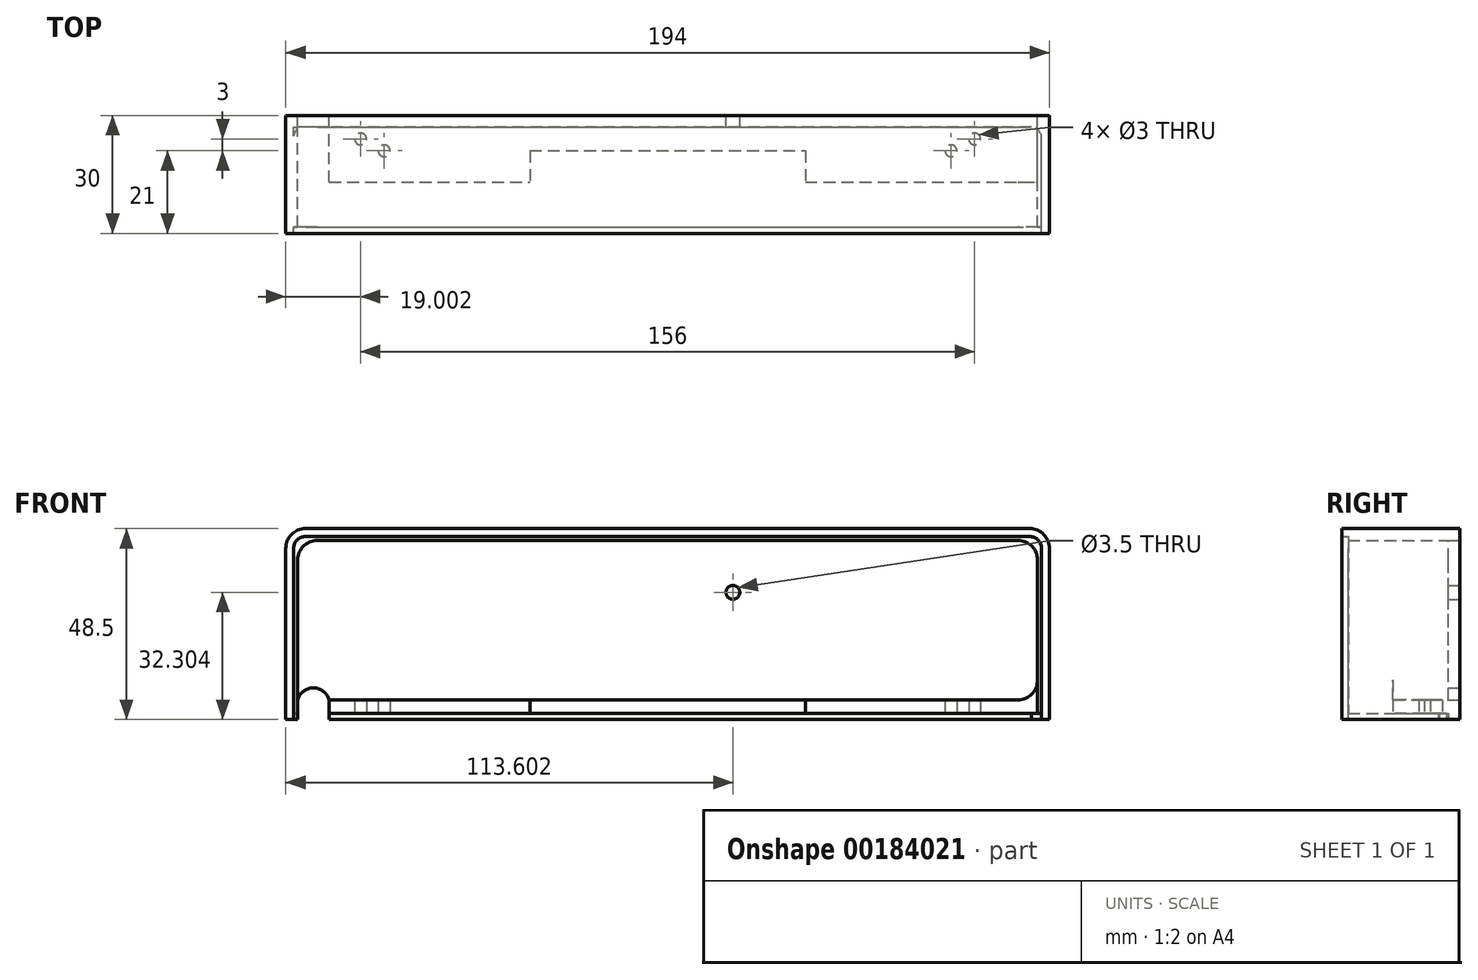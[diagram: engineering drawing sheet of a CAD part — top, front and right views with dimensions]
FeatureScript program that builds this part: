
annotation { "Feature Type Name" : "Feature", "Feature Type Description" : "" }
export const myFeature = defineFeature(function(context is Context, id is Id, definition is map)
    precondition{}
    {
        {
            var Q0;
            Q0=qCreatedBy(makeId("Front.planeOp"),FACE);
            var sketch = newSketch(context, id + "F0", { "sketchPlane" : qUnion([Q0])});
            skLineSegment(sketch, "E0", {"start": v(-180.48, -72.77) * mm, "end": v(-180.48, -29.27) * mm});
            skLineSegment(sketch, "E1", {"start": v(-175.48, -24.27) * mm, "end": v(8.52, -24.27) * mm});
            skLineSegment(sketch, "E2", {"start": v(13.52, -29.27) * mm, "end": v(13.52, -72.77) * mm});
            skLineSegment(sketch, "E3", {"start": v(13.52, -72.77) * mm, "end": v(11.52, -72.77) * mm});
            skLineSegment(sketch, "E4", {"start": v(11.52, -72.77) * mm, "end": v(11.52, -29.27) * mm});
            skLineSegment(sketch, "E5", {"start": v(-180.48, -72.77) * mm, "end": v(-177.48, -72.77) * mm});
            skLineSegment(sketch, "E6", {"start": v(-178.48, -72.77) * mm, "end": v(-178.48, -29.27) * mm});
            skLineSegment(sketch, "E7", {"start": v(-175.48, -26.27) * mm, "end": v(8.52, -26.27) * mm});
            skLineSegment(sketch, "E8", {"start": v(-169.48, -71.17) * mm, "end": v(11.52, -71.17) * mm});
            skLineSegment(sketch, "E9", {"start": v(-177.48, -72.77) * mm, "end": v(-177.48, -32.27) * mm});
            skLineSegment(sketch, "E10", {"start": v(-172.48, -27.27) * mm, "end": v(5.52, -27.27) * mm});
            skLineSegment(sketch, "E11", {"start": v(10.52, -62.77) * mm, "end": v(10.52, -32.27) * mm});
            skLineSegment(sketch, "E12", {"start": v(-169.48, -67.77) * mm, "end": v(5.52, -67.77) * mm});
            skLineSegment(sketch, "E13", {"start": v(-118.48, -71.17) * mm, "end": v(-118.48, -67.77) * mm});
            skLineSegment(sketch, "E14", {"start": v(-48.48, -71.17) * mm, "end": v(-48.48, -67.77) * mm});
            skLineSegment(sketch, "E15", {"start": v(-163.98, -67.77) * mm, "end": v(-163.98, -71.17) * mm});
            skLineSegment(sketch, "E16", {"start": v(-166.98, -67.77) * mm, "end": v(-166.98, -71.17) * mm});
            skLineSegment(sketch, "E17", {"start": v(-2.98, -67.77) * mm, "end": v(-2.98, -71.17) * mm});
            skLineSegment(sketch, "E18", {"start": v(0.02, -67.77) * mm, "end": v(0.02, -71.17) * mm});
            skArc(sketch, "E19", {"start": v(-175.48, -26.27) * mm, "mid": v(-177.6, -27.14) * mm, "end": v(-178.48, -29.27) * mm});
            skArc(sketch, "E20", {"start": v(11.52, -29.27) * mm, "mid": v(10.64, -27.14) * mm, "end": v(8.52, -26.27) * mm});
            skArc(sketch, "E21", {"start": v(-175.48, -24.27) * mm, "mid": v(-179.01, -25.73) * mm, "end": v(-180.48, -29.27) * mm});
            skArc(sketch, "E22", {"start": v(13.52, -29.27) * mm, "mid": v(12.06, -25.73) * mm, "end": v(8.52, -24.27) * mm});
            skLineSegment(sketch, "E23", {"start": v(-156.98, -71.17) * mm, "end": v(-156.98, -67.77) * mm});
            skLineSegment(sketch, "E24", {"start": v(-153.98, -71.17) * mm, "end": v(-153.98, -67.77) * mm});
            skLineSegment(sketch, "E25", {"start": v(-12.98, -67.77) * mm, "end": v(-12.98, -71.17) * mm});
            skLineSegment(sketch, "E26", {"start": v(-9.98, -67.77) * mm, "end": v(-9.98, -71.17) * mm});
            skLineSegment(sketch, "E27", {"start": v(11.52, -72.77) * mm, "end": v(-169.48, -72.77) * mm});
            skCircle(sketch, "E28", {"center": v(-66.88, -40.47) * mm, "radius": 1.75 * mm});
            skLineSegment(sketch, "E29", {"start": v(-169.48, -71.17) * mm, "end": v(-169.48, -67.77) * mm});
            skLineSegment(sketch, "E30", {"start": v(-169.48, -72.77) * mm, "end": v(-169.48, -67.77) * mm});
            skArc(sketch, "E31", {"start": v(-172.48, -27.27) * mm, "mid": v(-176.01, -28.73) * mm, "end": v(-177.48, -32.27) * mm});
            skArc(sketch, "E32", {"start": v(10.52, -32.27) * mm, "mid": v(9.06, -28.73) * mm, "end": v(5.52, -27.27) * mm});
            skArc(sketch, "E33", {"start": v(5.52, -67.77) * mm, "mid": v(9.06, -66.3) * mm, "end": v(10.52, -62.77) * mm});
            skArc(sketch, "E34", {"start": v(-169.48, -67.77) * mm, "mid": v(-173.48, -64.73) * mm, "end": v(-177.48, -67.77) * mm});
            skLineSegment(sketch, "E35", {"start": v(10.52, -62.77) * mm, "end": v(10.52, -71.17) * mm});
            skSolve(sketch);
        }
        {
            var Q0;
            {var subQ1=sQuery(id+"F0.wireOp",EDGE,"E0");Q0=makeQuery(id+"F0.imprint","IMPRINT",FACE,{"disambiguationData":[TD([[makeQuery(id+"F0.imprint","IMPRINT",EDGE,{"derivedFrom":subQ1}),-1.0]])]});}
            extrude(context, id + "F1", {"entities" : qUnion([Q0]), "depth" : 30 * mm});
        }
        {
            var Q0;
            {var subQ9=sQuery(id+"F0.wireOp",EDGE,"E6");Q0=makeQuery(id+"F0.imprint","IMPRINT",FACE,{"disambiguationData":[TD([[makeQuery(id+"F0.imprint","IMPRINT",EDGE,{"derivedFrom":subQ9}),-1.0]])]});}
            extrude(context, id + "F2", {"entities" : qUnion([Q0]), "operationType" : NewBodyOperationType.ADD, "depth" : 28.4 * mm});
        }
        {
            var Q0;
            {var subQ3=sQuery(id+"F0.wireOp",EDGE,"E16");Q0=makeQuery(id+"F0.imprint","IMPRINT",FACE,{"disambiguationData":[TD([[makeQuery(id+"F0.imprint","IMPRINT",EDGE,{"derivedFrom":subQ3}),-1.0]])]});}
            var Q1;
            {var subQ0=sQuery(id+"F0.wireOp",EDGE,"E15");Q1=makeQuery(id+"F0.imprint","IMPRINT",FACE,{"disambiguationData":[TD([[makeQuery(id+"F0.imprint","IMPRINT",EDGE,{"derivedFrom":subQ0}),-1.0]])]});}
            var Q2;
            {var subQ0=sQuery(id+"F0.wireOp",EDGE,"E15");Q2=makeQuery(id+"F0.imprint","IMPRINT",FACE,{"disambiguationData":[TD([[makeQuery(id+"F0.imprint","IMPRINT",EDGE,{"derivedFrom":subQ0}),1.0]])]});}
            var Q3;
            {var subQ0=sQuery(id+"F0.wireOp",EDGE,"E23");Q3=makeQuery(id+"F0.imprint","IMPRINT",FACE,{"disambiguationData":[TD([[makeQuery(id+"F0.imprint","IMPRINT",EDGE,{"derivedFrom":subQ0}),-1.0]])]});}
            var Q4;
            {var subQ0=sQuery(id+"F0.wireOp",EDGE,"E13");Q4=makeQuery(id+"F0.imprint","IMPRINT",FACE,{"disambiguationData":[TD([[makeQuery(id+"F0.imprint","IMPRINT",EDGE,{"derivedFrom":subQ0}),1.0]])]});}
            var Q5;
            {var subQ0=sQuery(id+"F0.wireOp",EDGE,"E13");Q5=makeQuery(id+"F0.imprint","IMPRINT",FACE,{"disambiguationData":[TD([[makeQuery(id+"F0.imprint","IMPRINT",EDGE,{"derivedFrom":subQ0}),-1.0]])]});}
            var Q6;
            {var subQ0=sQuery(id+"F0.wireOp",EDGE,"E14");Q6=makeQuery(id+"F0.imprint","IMPRINT",FACE,{"disambiguationData":[TD([[makeQuery(id+"F0.imprint","IMPRINT",EDGE,{"derivedFrom":subQ0}),-1.0]])]});}
            var Q7;
            {var subQ0=sQuery(id+"F0.wireOp",EDGE,"E25");Q7=makeQuery(id+"F0.imprint","IMPRINT",FACE,{"disambiguationData":[TD([[makeQuery(id+"F0.imprint","IMPRINT",EDGE,{"derivedFrom":subQ0}),1.0]])]});}
            var Q8;
            {var subQ0=sQuery(id+"F0.wireOp",EDGE,"E17");Q8=makeQuery(id+"F0.imprint","IMPRINT",FACE,{"disambiguationData":[TD([[makeQuery(id+"F0.imprint","IMPRINT",EDGE,{"derivedFrom":subQ0}),-1.0]])]});}
            var Q9;
            {var subQ0=sQuery(id+"F0.wireOp",EDGE,"E17");Q9=makeQuery(id+"F0.imprint","IMPRINT",FACE,{"disambiguationData":[TD([[makeQuery(id+"F0.imprint","IMPRINT",EDGE,{"derivedFrom":subQ0}),1.0]])]});}
            var Q10;
            {var subQ1=sQuery(id+"F0.wireOp",EDGE,"E18");Q10=makeQuery(id+"F0.imprint","IMPRINT",FACE,{"disambiguationData":[TD([[makeQuery(id+"F0.imprint","IMPRINT",EDGE,{"derivedFrom":subQ1}),1.0]])]});}
            extrude(context, id + "F3", {"entities" : qUnion([Q0, Q1, Q2, Q3, Q4, Q5, Q6, Q7, Q8, Q9, Q10]), "operationType" : NewBodyOperationType.ADD, "depth" : 17 * mm});
        }
        {
            var Q0;
            {var subQ8=sQuery(id+"F0.wireOp",EDGE,"E27");Q0=makeQuery(id+"F0.imprint","IMPRINT",FACE,{"disambiguationData":[TD([[makeQuery(id+"F0.imprint","IMPRINT",EDGE,{"derivedFrom":subQ8}),-1.0]])]});}
            var Q1;
            Q1=makeQuery(id+"F0.imprint","IMPRINT",FACE,{"disambiguationData":[TD([[makeQuery(id+"F0.imprint","IMPRINT",EDGE,{"derivedFrom":sQuery(id+"F0.wireOp",EDGE,"E10")}),-1.0]])]});
            extrude(context, id + "F4", {"entities" : qUnion([Q0, Q1]), "depth" : 3 * mm});
        }
        {
            var Q0;
            Q0=qCreatedBy(makeId("Top.planeOp"),FACE);
            cPlane(context, id + "F5", {"entities" : qUnion([Q0]), "cplaneType" : CPlaneType.OFFSET, "offset" : 72.77 * mm, "oppositeDirection" : true, "width" : 150 * mm, "height" : 150 * mm});
        }
        {
            var Q0;
            Q0=qCreatedBy(id+"F5.planeOp",FACE);
            var sketch = newSketch(context, id + "F6", { "sketchPlane" : qUnion([Q0])});
            skLineSegment(sketch, "E36", {"start": v(-172.95, 16.86) * mm, "end": v(-172.95, 31.58) * mm});
            skLineSegment(sketch, "E37", {"start": v(-172.95, 31.58) * mm, "end": v(5.1, 31.58) * mm});
            skLineSegment(sketch, "E38", {"start": v(-172.95, 16.86) * mm, "end": v(-121.99, 16.86) * mm});
            skLineSegment(sketch, "E39", {"start": v(-121.99, 16.86) * mm, "end": v(-121.99, 24.49) * mm});
            skLineSegment(sketch, "E40", {"start": v(-121.99, 24.49) * mm, "end": v(-51.99, 24.49) * mm});
            skLineSegment(sketch, "E41", {"start": v(-51.99, 24.49) * mm, "end": v(-51.99, 16.86) * mm});
            skLineSegment(sketch, "E42", {"start": v(-51.99, 16.86) * mm, "end": v(8.01, 16.86) * mm});
            skLineSegment(sketch, "E43", {"start": v(8.01, 16.86) * mm, "end": v(8.01, 28.3) * mm});
            skCircle(sketch, "E44", {"center": v(-5.48, -6) * mm, "radius": 1.5 * mm});
            skCircle(sketch, "E45", {"center": v(-11.48, -9) * mm, "radius": 1.5 * mm});
            skCircle(sketch, "E46", {"center": v(-164.87, 28.02) * mm, "radius": 1.5 * mm});
            skCircle(sketch, "E47", {"center": v(-158.87, 24.43) * mm, "radius": 1.5 * mm});
            skArc(sketch, "E48", {"start": v(8.1, 28.44) * mm, "mid": v(7.22, 30.56) * mm, "end": v(5.09, 31.44) * mm});
            skLineSegment(sketch, "E49.bottom", {"start": v(-48.48, -22.9) * mm, "end": v(-118.48, -22.9) * mm});
            skLineSegment(sketch, "E49.top", {"start": v(-48.48, -9) * mm, "end": v(-118.48, -9) * mm});
            skLineSegment(sketch, "E49.left", {"start": v(-48.48, -22.9) * mm, "end": v(-48.48, -9) * mm});
            skLineSegment(sketch, "E49.right", {"start": v(-118.48, -22.9) * mm, "end": v(-118.48, -9) * mm});
            skCircle(sketch, "E50", {"center": v(-155.48, -9) * mm, "radius": 1.5 * mm});
            skCircle(sketch, "E51", {"center": v(-161.48, -6) * mm, "radius": 1.5 * mm});
            skArc(sketch, "E52", {"start": v(11.52, -5.57) * mm, "mid": v(10.7, -3.73) * mm, "end": v(8.84, -3) * mm});
            skLineSegment(sketch, "E53", {"start": v(11.52, -5.57) * mm, "end": v(11.52, -3) * mm});
            skLineSegment(sketch, "E54", {"start": v(11.52, -3) * mm, "end": v(8.84, -3) * mm});
            skLineSegment(sketch, "E55.MirrorCS", {"start": v(-178.48, -2.96) * mm, "end": v(-177.48, -2.94) * mm});
            skLineSegment(sketch, "E56.MirrorCS", {"start": v(-178.48, -5.27) * mm, "end": v(-178.48, -2.96) * mm});
            skArc(sketch, "E57.MirrorCS", {"start": v(-178.48, -5.27) * mm, "mid": v(-178.17, -4.26) * mm, "end": v(-177.48, -3.45) * mm});
            skLineSegment(sketch, "E58", {"start": v(-178.48, -5.27) * mm, "end": v(-178.48, -28.4) * mm});
            skLineSegment(sketch, "E59", {"start": v(-178.48, -28.4) * mm, "end": v(-177.48, -28.4) * mm});
            skLineSegment(sketch, "E60", {"start": v(-177.48, -28.4) * mm, "end": v(-177.48, -2.94) * mm});
            skSolve(sketch);
        }
        {
            var Q0;
            Q0=makeQuery(id+"F6.imprint","IMPRINT",FACE,{"disambiguationData":[TD([[makeQuery(id+"F6.imprint","IMPRINT",EDGE,{"derivedFrom":sQuery(id+"F6.wireOp",EDGE,"E45")}),1.0]])]});
            var Q1;
            Q1=makeQuery(id+"F6.imprint","IMPRINT",FACE,{"disambiguationData":[TD([[makeQuery(id+"F6.imprint","IMPRINT",EDGE,{"derivedFrom":sQuery(id+"F6.wireOp",EDGE,"E44")}),1.0]])]});
            var Q2;
            Q2=makeQuery(id+"F6.imprint","IMPRINT",FACE,{"disambiguationData":[TD([[makeQuery(id+"F6.imprint","IMPRINT",EDGE,{"derivedFrom":sQuery(id+"F6.wireOp",EDGE,"E49.bottom")}),-1.0]])]});
            var Q3;
            Q3=makeQuery(id+"F6.imprint","IMPRINT",FACE,{"disambiguationData":[TD([[makeQuery(id+"F6.imprint","IMPRINT",EDGE,{"derivedFrom":sQuery(id+"F6.wireOp",EDGE,"E51")}),1.0]])]});
            var Q4;
            Q4=makeQuery(id+"F6.imprint","IMPRINT",FACE,{"disambiguationData":[TD([[makeQuery(id+"F6.imprint","IMPRINT",EDGE,{"derivedFrom":sQuery(id+"F6.wireOp",EDGE,"E50")}),1.0]])]});
            var Q5;
            Q5=sQuery(id+"F6.wireOp",EDGE,"E45");
            var Q6;
            Q6=sQuery(id+"F6.wireOp",EDGE,"E44");
            extrude(context, id + "F7", {"entities" : qUnion([Q0, Q1, Q2, Q3, Q4]), "operationType" : NewBodyOperationType.REMOVE, "surfaceEntities" : qUnion([Q5, Q6]), "depth" : 25 * mm});
        }
        {
            var Q0;
            {var subQ0=sQuery(id+"F6.wireOp",EDGE,"E53");Q0=makeQuery(id+"F6.imprint","IMPRINT",FACE,{"disambiguationData":[TD([[makeQuery(id+"F6.imprint","IMPRINT",EDGE,{"derivedFrom":subQ0}),1.0]])]});}
            extrude(context, id + "F8", {"entities" : qUnion([Q0]), "operationType" : NewBodyOperationType.ADD, "depth" : 3 * mm});
        }
        {
            var Q0;
            {var subQ0=sQuery(id+"F6.wireOp",EDGE,"E57.MirrorCS");Q0=makeQuery(id+"F6.imprint","IMPRINT",FACE,{"disambiguationData":[TD([[makeQuery(id+"F6.imprint","IMPRINT",EDGE,{"derivedFrom":subQ0}),-1.0]])]});}
            extrude(context, id + "F9", {"entities" : qUnion([Q0]), "operationType" : NewBodyOperationType.REMOVE, "depth" : 1.6 * mm});
        }
    });
